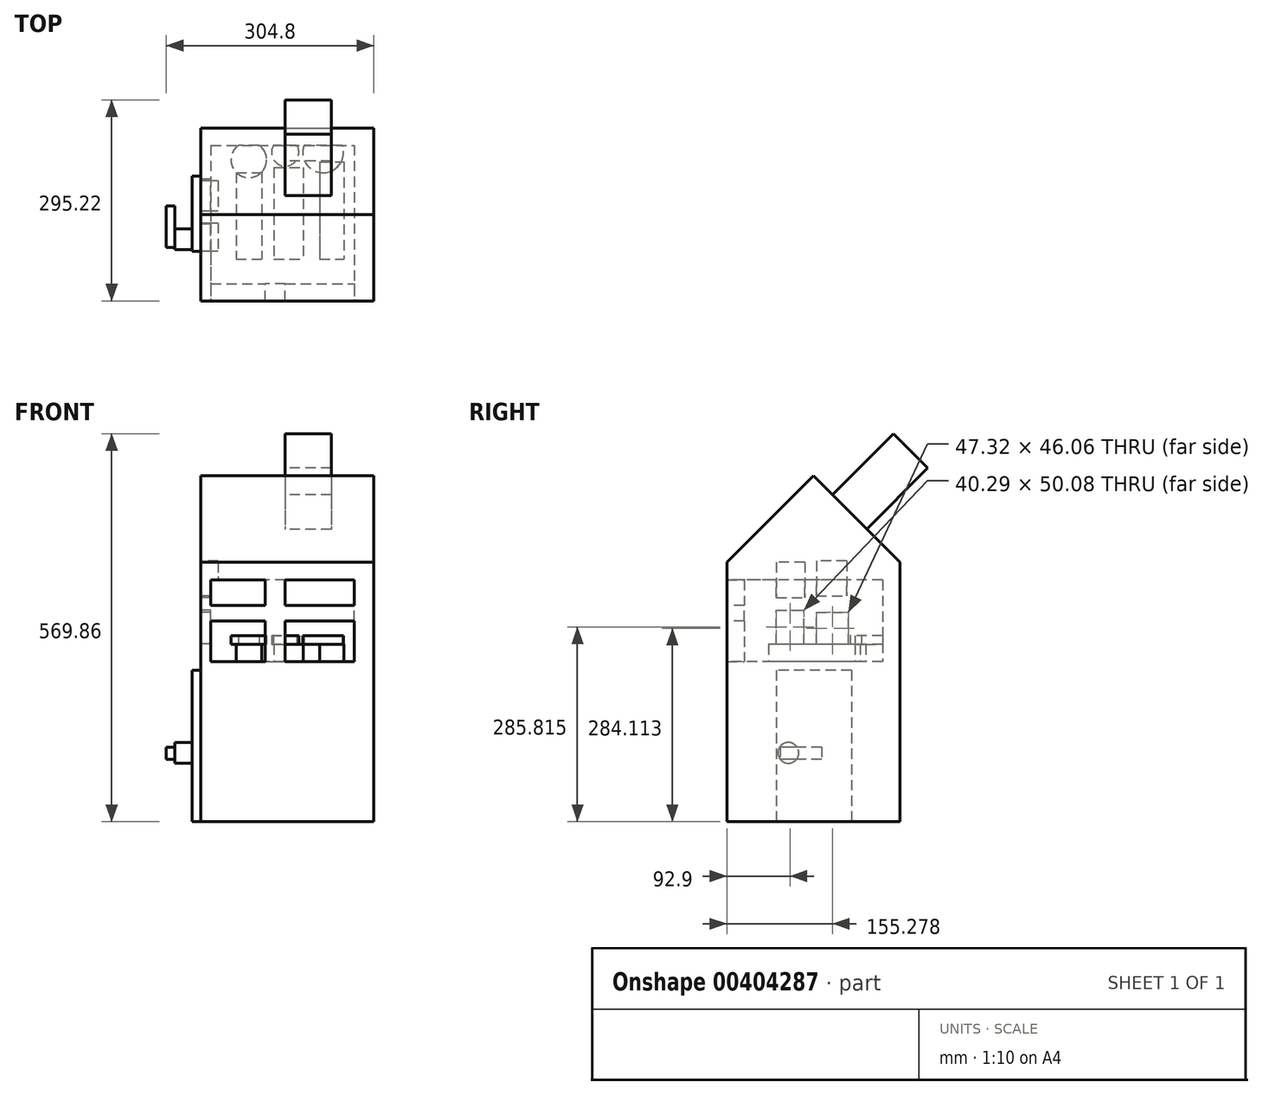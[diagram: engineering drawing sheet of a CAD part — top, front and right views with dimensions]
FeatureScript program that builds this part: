
annotation { "Feature Type Name" : "Feature", "Feature Type Description" : "" }
export const myFeature = defineFeature(function(context is Context, id is Id, definition is map)
    precondition{}
    {
        {
            var Q0;
            Q0=qCreatedBy(makeId("Top.planeOp"),FACE);
            var sketch = newSketch(context, id + "F0", { "sketchPlane" : qUnion([Q0])});
            skLineSegment(sketch, "E0.bottom", {"start": v(-123.84, 122.38) * mm, "end": v(130.16, 122.38) * mm});
            skLineSegment(sketch, "E0.top", {"start": v(-123.84, -131.62) * mm, "end": v(130.16, -131.62) * mm});
            skLineSegment(sketch, "E0.left", {"start": v(-123.84, 122.38) * mm, "end": v(-123.84, -131.62) * mm});
            skLineSegment(sketch, "E0.right", {"start": v(130.16, 122.38) * mm, "end": v(130.16, -131.62) * mm});
            skSolve(sketch);
        }
        {
            var Q0;
            Q0 = qSketchRegion(id + "F0", true);
            extrude(context, id + "F1", {"entities" : qUnion([Q0]), "depth" : 508 * mm});
        }
        {
            var Q0;
            Q0=makeQuery(id+"F1.opExtrude","CAP_EDGE",EDGE,{"disambiguationData":[OSD([sQuery(id+"F0.wireOp",EDGE,"E0.top")])],"isStart":false});
            chamfer(context, id + "F2", {"entities" : qUnion([Q0]), "width" : 127 * mm, "tangentPropagation" : true});
        }
        {
            var Q0;
            Q0=makeQuery(id+"F1.opExtrude","CAP_EDGE",EDGE,{"disambiguationData":[OSD([sQuery(id+"F0.wireOp",EDGE,"E0.bottom")])],"isStart":false});
            chamfer(context, id + "F3", {"entities" : qUnion([Q0]), "width" : 127 * mm, "tangentPropagation" : true});
        }
        {
            var Q0;
            Q0=makeQuery(id+"F1.opExtrude","SWEPT_FACE",FACE,{"disambiguationData":[OSD([sQuery(id+"F0.wireOp",EDGE,"E0.left")])]});
            var sketch = newSketch(context, id + "F4", { "sketchPlane" : qUnion([Q0])});
            skLineSegment(sketch, "E1.bottom", {"start": v(-51.39, 222.2) * mm, "end": v(58.86, 222.2) * mm});
            skLineSegment(sketch, "E1.top", {"start": v(-51.39, 0) * mm, "end": v(58.86, 0) * mm});
            skLineSegment(sketch, "E1.left", {"start": v(-51.39, 222.2) * mm, "end": v(-51.39, 0) * mm});
            skLineSegment(sketch, "E1.right", {"start": v(58.86, 222.2) * mm, "end": v(58.86, 0) * mm});
            skSolve(sketch);
        }
        {
            var Q0;
            Q0 = qSketchRegion(id + "F4", true);
            extrude(context, id + "F5", {"entities" : qUnion([Q0]), "operationType" : NewBodyOperationType.ADD, "depth" : 12.7 * mm});
        }
        {
            var Q0;
            Q0=makeQuery(id+"F5.opExtrude","CAP_FACE",FACE,{"disambiguationData":[OSD([sQuery(id+"F4.wireOp",EDGE,"E1.bottom"),sQuery(id+"F4.wireOp",EDGE,"E1.top"),sQuery(id+"F4.wireOp",EDGE,"E1.left"),sQuery(id+"F4.wireOp",EDGE,"E1.right")])],"isStart":false});
            var sketch = newSketch(context, id + "F6", { "sketchPlane" : qUnion([Q0])});
            skCircle(sketch, "E2", {"center": v(41.21, 101.07) * mm, "radius": 15.24 * mm});
            skSolve(sketch);
        }
        {
            var Q0;
            Q0 = qSketchRegion(id + "F6", true);
            extrude(context, id + "F7", {"entities" : qUnion([Q0]), "operationType" : NewBodyOperationType.ADD, "depth" : 25.4 * mm});
        }
        {
            var Q0;
            Q0=makeQuery(id+"F7.opExtrude","CAP_FACE",FACE,{"disambiguationData":[OSD([sQuery(id+"F6.wireOp",EDGE,"E2")])],"isStart":false});
            var sketch = newSketch(context, id + "F8", { "sketchPlane" : qUnion([Q0])});
            skLineSegment(sketch, "E3.bottom", {"start": v(-7.65, 109.48) * mm, "end": v(53.24, 109.48) * mm});
            skLineSegment(sketch, "E3.top", {"start": v(-7.65, 91.7) * mm, "end": v(53.24, 91.7) * mm});
            skLineSegment(sketch, "E3.left", {"start": v(-7.65, 109.48) * mm, "end": v(-7.65, 91.7) * mm});
            skLineSegment(sketch, "E3.right", {"start": v(53.24, 109.48) * mm, "end": v(53.24, 91.7) * mm});
            skSolve(sketch);
        }
        {
            var Q0;
            Q0 = qSketchRegion(id + "F8", true);
            extrude(context, id + "F9", {"entities" : qUnion([Q0]), "operationType" : NewBodyOperationType.ADD, "depth" : 12.7 * mm});
        }
        {
            var Q0;
            Q0=makeQuery(id+"F1.opExtrude","SWEPT_FACE",FACE,{"disambiguationData":[OSD([sQuery(id+"F0.wireOp",EDGE,"E0.left")])]});
            var sketch = newSketch(context, id + "F10", { "sketchPlane" : qUnion([Q0])});
            skLineSegment(sketch, "E4.bottom", {"start": v(-44.42, 382.95) * mm, "end": v(0, 382.95) * mm});
            skLineSegment(sketch, "E4.top", {"start": v(-44.42, 331.27) * mm, "end": v(0, 331.27) * mm});
            skLineSegment(sketch, "E4.left", {"start": v(-44.42, 382.95) * mm, "end": v(-44.42, 331.27) * mm});
            skLineSegment(sketch, "E4.right", {"start": v(0, 382.95) * mm, "end": v(0, 331.27) * mm});
            skLineSegment(sketch, "E5.bottom", {"start": v(-47.32, 307.14) * mm, "end": v(0, 307.14) * mm});
            skLineSegment(sketch, "E5.top", {"start": v(-47.32, 261.08) * mm, "end": v(0, 261.08) * mm});
            skLineSegment(sketch, "E5.left", {"start": v(-47.32, 307.14) * mm, "end": v(-47.32, 261.08) * mm});
            skLineSegment(sketch, "E5.right", {"start": v(0, 307.14) * mm, "end": v(0, 261.08) * mm});
            skLineSegment(sketch, "E6.bottom", {"start": v(17.27, 381) * mm, "end": v(58.84, 381) * mm});
            skLineSegment(sketch, "E6.top", {"start": v(17.27, 329.11) * mm, "end": v(58.84, 329.11) * mm});
            skLineSegment(sketch, "E6.left", {"start": v(17.27, 381) * mm, "end": v(17.27, 329.11) * mm});
            skLineSegment(sketch, "E6.right", {"start": v(58.84, 381) * mm, "end": v(58.84, 329.11) * mm});
            skLineSegment(sketch, "E7.bottom", {"start": v(18.58, 310.85) * mm, "end": v(58.86, 310.85) * mm});
            skLineSegment(sketch, "E7.top", {"start": v(18.58, 260.78) * mm, "end": v(58.86, 260.78) * mm});
            skLineSegment(sketch, "E7.left", {"start": v(18.58, 310.85) * mm, "end": v(18.58, 260.78) * mm});
            skLineSegment(sketch, "E7.right", {"start": v(58.86, 310.85) * mm, "end": v(58.86, 260.78) * mm});
            skSolve(sketch);
        }
        {
            var Q0;
            Q0 = qSketchRegion(id + "F10", true);
            extrude(context, id + "F11", {"entities" : qUnion([Q0]), "operationType" : NewBodyOperationType.REMOVE, "oppositeDirection" : true, "depth" : 25.4 * mm});
        }
        {
            var Q0;
            Q0=makeQuery(id+"F3.opChamfer","BLEND_FACE",FACE,{"disambiguationData":[OSD([sQuery(id+"F0.wireOp",EDGE,"E0.bottom")])]});
            var sketch = newSketch(context, id + "F12", { "sketchPlane" : qUnion([Q0])});
            skLineSegment(sketch, "E8.bottom", {"start": v(-67.73, 322.95) * mm, "end": v(0, 322.95) * mm});
            skLineSegment(sketch, "E8.top", {"start": v(-67.73, 251.58) * mm, "end": v(0, 251.58) * mm});
            skLineSegment(sketch, "E8.left", {"start": v(-67.73, 322.95) * mm, "end": v(-67.73, 251.58) * mm});
            skLineSegment(sketch, "E8.right", {"start": v(0, 322.95) * mm, "end": v(0, 251.58) * mm});
            skSolve(sketch);
        }
        {
            var Q0;
            Q0 = qSketchRegion(id + "F12", true);
            extrude(context, id + "F13", {"entities" : qUnion([Q0]), "operationType" : NewBodyOperationType.ADD, "depth" : 127 * mm});
        }
        {
            var Q0;
            Q0=makeQuery(id+"F1.opExtrude","SWEPT_FACE",FACE,{"disambiguationData":[OSD([sQuery(id+"F0.wireOp",EDGE,"E0.top")])]});
            var sketch = newSketch(context, id + "F14", { "sketchPlane" : qUnion([Q0])});
            skLineSegment(sketch, "E9.bottom", {"start": v(-109.1, 354.76) * mm, "end": v(101.2, 354.76) * mm});
            skLineSegment(sketch, "E9.top", {"start": v(-109.1, 234.77) * mm, "end": v(101.2, 234.77) * mm});
            skLineSegment(sketch, "E9.left", {"start": v(-109.1, 354.76) * mm, "end": v(-109.1, 234.77) * mm});
            skLineSegment(sketch, "E9.right", {"start": v(101.2, 354.76) * mm, "end": v(101.2, 234.77) * mm});
            skSolve(sketch);
        }
        {
            var Q0;
            Q0 = qSketchRegion(id + "F14", true);
            extrude(context, id + "F15", {"entities" : qUnion([Q0]), "operationType" : NewBodyOperationType.REMOVE, "oppositeDirection" : true, "depth" : 228.6 * mm});
        }
        {
            var Q0;
            Q0=makeQuery(id+"F15.boolean.opBoolean","COPY",FACE,{"derivedFrom":makeQuery(id+"F15.opExtrude","SWEPT_FACE",FACE,{"disambiguationData":[OSD([sQuery(id+"F14.wireOp",EDGE,"E9.top")])]})});
            var sketch = newSketch(context, id + "F16", { "sketchPlane" : qUnion([Q0])});
            skLineSegment(sketch, "E10.bottom", {"start": v(-72.2, 56.68) * mm, "end": v(-34.56, 56.68) * mm});
            skLineSegment(sketch, "E10.top", {"start": v(-72.2, -70.3) * mm, "end": v(-34.56, -70.3) * mm});
            skLineSegment(sketch, "E10.left", {"start": v(-72.2, 56.68) * mm, "end": v(-72.2, -70.3) * mm});
            skLineSegment(sketch, "E10.right", {"start": v(-34.56, 56.68) * mm, "end": v(-34.56, -70.3) * mm});
            skLineSegment(sketch, "E11.bottom", {"start": v(-16.72, 64.17) * mm, "end": v(26.46, 64.17) * mm});
            skLineSegment(sketch, "E11.top", {"start": v(-16.72, -70.3) * mm, "end": v(26.46, -70.3) * mm});
            skLineSegment(sketch, "E11.left", {"start": v(-16.72, 64.17) * mm, "end": v(-16.72, -70.3) * mm});
            skLineSegment(sketch, "E11.right", {"start": v(26.46, 64.17) * mm, "end": v(26.46, -70.3) * mm});
            skLineSegment(sketch, "E12.bottom", {"start": v(50.81, 72.73) * mm, "end": v(86.04, 72.73) * mm});
            skLineSegment(sketch, "E12.top", {"start": v(50.81, -70.3) * mm, "end": v(86.04, -70.3) * mm});
            skLineSegment(sketch, "E12.left", {"start": v(50.81, 72.73) * mm, "end": v(50.81, -70.3) * mm});
            skLineSegment(sketch, "E12.right", {"start": v(86.04, 72.73) * mm, "end": v(86.04, -70.3) * mm});
            skSolve(sketch);
        }
        {
            var Q0;
            Q0 = qSketchRegion(id + "F16", true);
            extrude(context, id + "F17", {"entities" : qUnion([Q0]), "operationType" : NewBodyOperationType.ADD, "depth" : 25.4 * mm});
        }
        {
            var Q0;
            Q0=makeQuery(id+"F17.opExtrude","CAP_FACE",FACE,{"disambiguationData":[OSD([sQuery(id+"F16.wireOp",EDGE,"E10.bottom"),sQuery(id+"F16.wireOp",EDGE,"E10.top"),sQuery(id+"F16.wireOp",EDGE,"E10.left"),sQuery(id+"F16.wireOp",EDGE,"E10.right")])],"isStart":false});
            var sketch = newSketch(context, id + "F18", { "sketchPlane" : qUnion([Q0])});
            skCircle(sketch, "E13", {"center": v(-53.38, 75.65) * mm, "radius": 26.13 * mm});
            skPoint(sketch, "E13.centerSnap0", {"position": v(-53.38, 56.68) * mm});
            skCircle(sketch, "E14", {"center": v(0, 86.52) * mm, "radius": 20.07 * mm});
            skCircle(sketch, "E15", {"center": v(55.74, 86.52) * mm, "radius": 29.93 * mm});
            skSolve(sketch);
        }
        {
            var Q0;
            Q0 = qSketchRegion(id + "F18", true);
            extrude(context, id + "F19", {"entities" : qUnion([Q0]), "operationType" : NewBodyOperationType.ADD, "depth" : 12.7 * mm});
        }
        {
            var Q0;
            Q0=makeQuery(id+"F1.opExtrude","SWEPT_FACE",FACE,{"disambiguationData":[OSD([sQuery(id+"F0.wireOp",EDGE,"E0.top")])]});
            var sketch = newSketch(context, id + "F20", { "sketchPlane" : qUnion([Q0])});
            skLineSegment(sketch, "E16.bottom", {"start": v(-29.21, 381) * mm, "end": v(0, 381) * mm});
            skLineSegment(sketch, "E16.top", {"start": v(-29.21, 217.91) * mm, "end": v(0, 217.91) * mm});
            skLineSegment(sketch, "E16.left", {"start": v(-29.21, 381) * mm, "end": v(-29.21, 217.91) * mm});
            skLineSegment(sketch, "E16.right", {"start": v(0, 381) * mm, "end": v(0, 217.91) * mm});
            skPoint(sketch, "E17.firstSnap0", {"position": v(-109.1, 294.77) * mm});
            skLineSegment(sketch, "E17.bottom", {"start": v(-123.84, 294.77) * mm, "end": v(130.16, 294.77) * mm});
            skLineSegment(sketch, "E17.top", {"start": v(-123.84, 317.9) * mm, "end": v(130.16, 317.9) * mm});
            skLineSegment(sketch, "E17.left", {"start": v(-123.84, 294.77) * mm, "end": v(-123.84, 317.9) * mm});
            skLineSegment(sketch, "E17.right", {"start": v(130.16, 294.77) * mm, "end": v(130.16, 317.9) * mm});
            skSolve(sketch);
        }
        {
            var Q0;
            Q0 = qSketchRegion(id + "F20", true);
            extrude(context, id + "F21", {"entities" : qUnion([Q0]), "operationType" : NewBodyOperationType.ADD, "oppositeDirection" : true, "depth" : 25.4 * mm});
        }
    });
